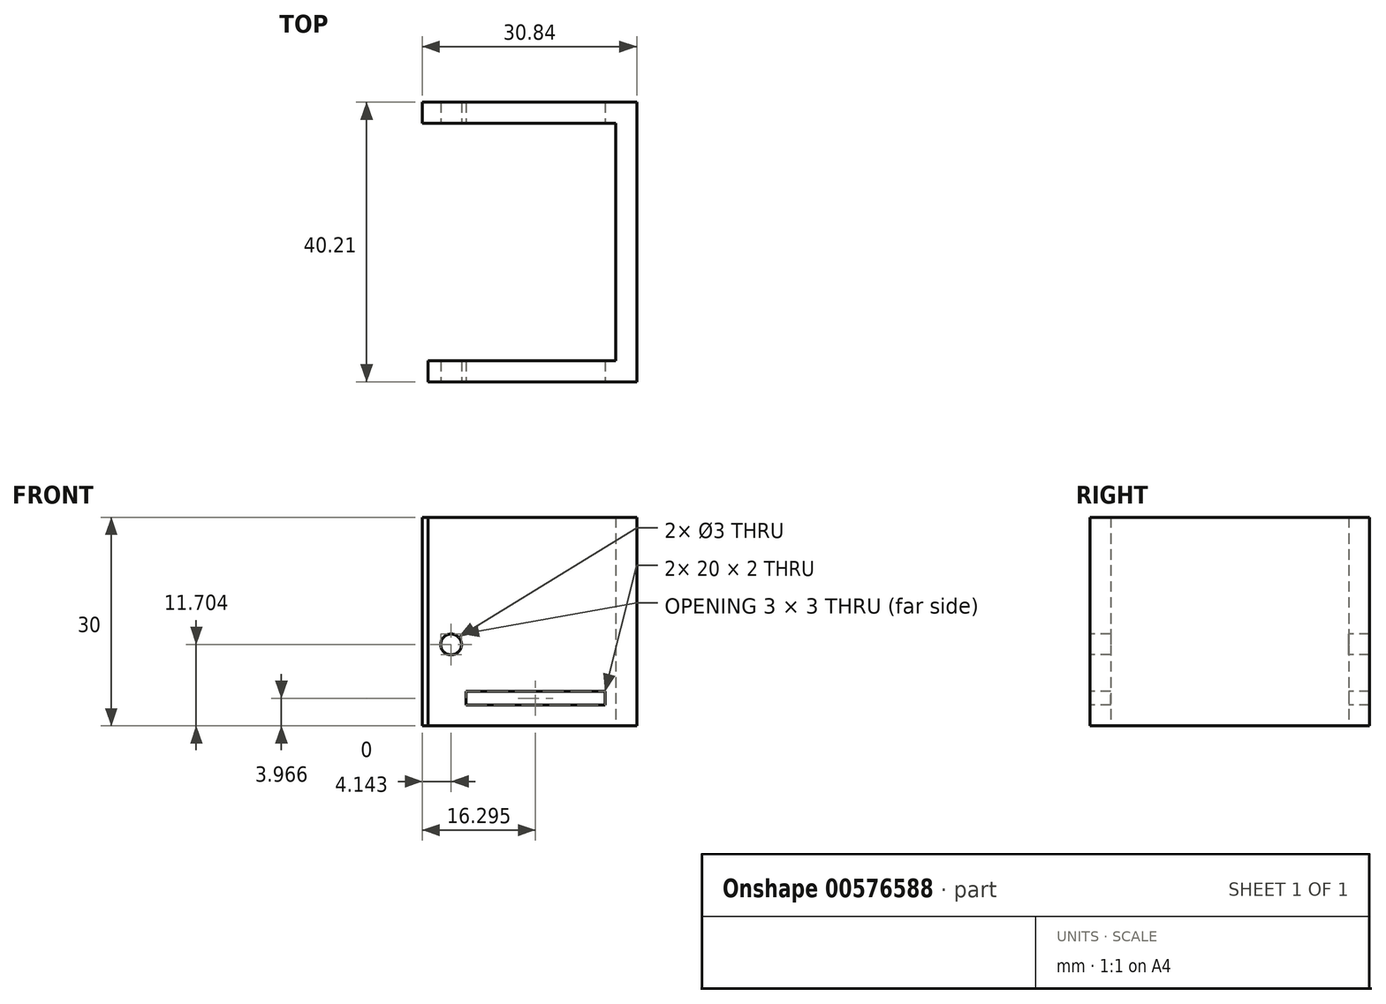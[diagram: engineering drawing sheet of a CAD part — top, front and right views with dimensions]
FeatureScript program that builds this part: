
annotation { "Feature Type Name" : "Feature", "Feature Type Description" : "" }
export const myFeature = defineFeature(function(context is Context, id is Id, definition is map)
    precondition{}
    {
        {
            var Q0;
            Q0=qCreatedBy(makeId("Top.planeOp"),FACE);
            var sketch = newSketch(context, id + "F0", { "sketchPlane" : qUnion([Q0])});
            skLineSegment(sketch, "E0", {"start": v(-33.87, 13.89) * mm, "end": v(-33.87, 16.89) * mm});
            skLineSegment(sketch, "E1", {"start": v(-33.87, 16.89) * mm, "end": v(-3.03, 16.89) * mm});
            skLineSegment(sketch, "E2", {"start": v(-3.03, 16.89) * mm, "end": v(-3.03, -23.32) * mm});
            skLineSegment(sketch, "E3", {"start": v(-3.03, -23.32) * mm, "end": v(-33.03, -23.32) * mm});
            skLineSegment(sketch, "E4", {"start": v(-33.03, -23.32) * mm, "end": v(-33.03, -20.32) * mm});
            skLineSegment(sketch, "E5", {"start": v(-33.03, -20.32) * mm, "end": v(-6.03, -20.32) * mm});
            skLineSegment(sketch, "E6", {"start": v(-6.03, -20.32) * mm, "end": v(-6.03, 13.89) * mm});
            skLineSegment(sketch, "E7", {"start": v(-6.03, 13.89) * mm, "end": v(-33.87, 13.89) * mm});
            skSolve(sketch);
        }
        {
            var Q0;
            Q0 = qSketchRegion(id + "F0", true);
            extrude(context, id + "F1", {"entities" : qUnion([Q0]), "depth" : 30 * mm, "offsetDistance" : 25 * mm});
        }
        {
            var Q0;
            Q0=makeQuery(id+"F1.opExtrude","SWEPT_FACE",FACE,{"disambiguationData":[OSD([sQuery(id+"F0.wireOp",EDGE,"E3")])]});
            var sketch = newSketch(context, id + "F2", { "sketchPlane" : qUnion([Q0])});
            skLineSegment(sketch, "E8.bottom", {"start": v(-27.58, 4.97) * mm, "end": v(-7.58, 4.97) * mm});
            skLineSegment(sketch, "E8.top", {"start": v(-27.58, 2.97) * mm, "end": v(-7.58, 2.97) * mm});
            skLineSegment(sketch, "E8.left", {"start": v(-27.58, 4.97) * mm, "end": v(-27.58, 2.97) * mm});
            skLineSegment(sketch, "E8.right", {"start": v(-7.58, 4.97) * mm, "end": v(-7.58, 2.97) * mm});
            skCircle(sketch, "E9", {"center": v(-29.73, 11.7) * mm, "radius": 1.5 * mm});
            skSolve(sketch);
        }
        {
            var Q0;
            Q0 = qSketchRegion(id + "F2", true);
            var Q1;
            Q1=makeQuery(id+"F1.opExtrude","SWEPT_FACE",FACE,{"disambiguationData":[OSD([sQuery(id+"F0.wireOp",EDGE,"E1")])]});
            extrude(context, id + "F3", {"entities" : qUnion([Q0]), "operationType" : NewBodyOperationType.REMOVE, "endBound" : BoundingType.UP_TO_SURFACE, "oppositeDirection" : true, "depth" : 25 * mm, "endBoundEntityFace" : qUnion([Q1]), "offsetDistance" : 25 * mm});
        }
    });
